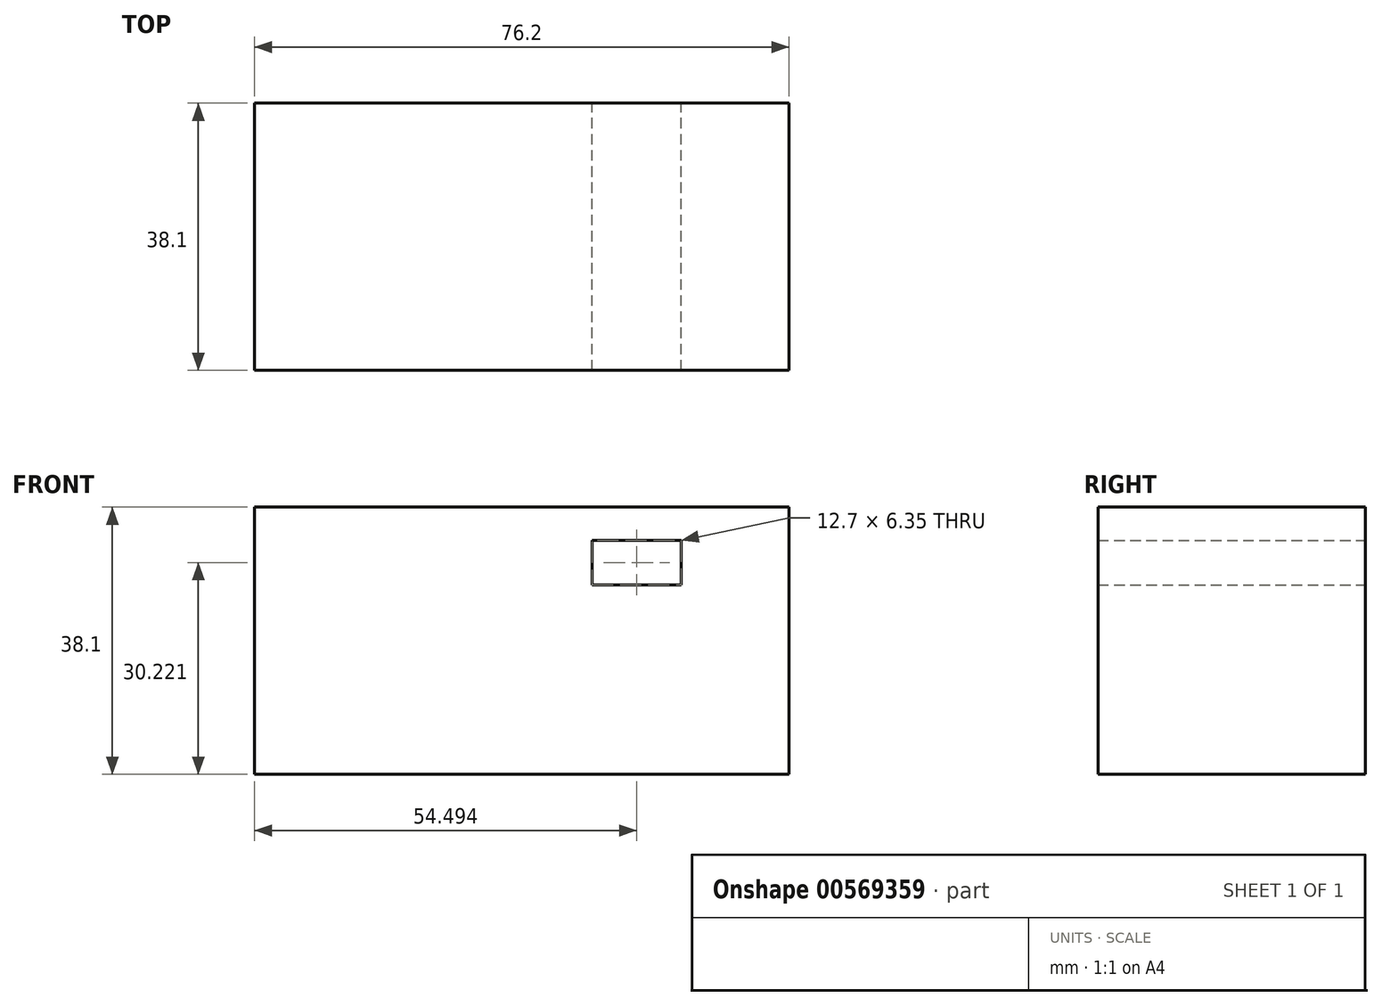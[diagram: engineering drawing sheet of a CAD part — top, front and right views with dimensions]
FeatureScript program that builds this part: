
annotation { "Feature Type Name" : "Feature", "Feature Type Description" : "" }
export const myFeature = defineFeature(function(context is Context, id is Id, definition is map)
    precondition{}
    {
        {
            var Q0;
            Q0=qCreatedBy(makeId("Front.planeOp"),FACE);
            var sketch = newSketch(context, id + "F0", { "sketchPlane" : qUnion([Q0])});
            skLineSegment(sketch, "E0.bottom", {"start": v(38.1, 19.05) * mm, "end": v(-38.1, 19.05) * mm});
            skLineSegment(sketch, "E0.top", {"start": v(38.1, -19.05) * mm, "end": v(-38.1, -19.05) * mm});
            skLineSegment(sketch, "E0.left", {"start": v(38.1, 19.05) * mm, "end": v(38.1, -19.05) * mm});
            skLineSegment(sketch, "E0.right", {"start": v(-38.1, 19.05) * mm, "end": v(-38.1, -19.05) * mm});
            skPoint(sketch, "E0.middle", {"position": v(0, 0) * mm});
            skSolve(sketch);
        }
        {
            var Q0;
            Q0=makeQuery(id+"F0.imprint","IMPRINT",FACE,{"disambiguationData":[TD([[makeQuery(id+"F0.imprint","IMPRINT",EDGE,{"derivedFrom":sQuery(id+"F0.wireOp",EDGE,"E0.bottom")}),1.0]])]});
            var sketch = newSketch(context, id + "F1", { "sketchPlane" : qUnion([Q0])});
            skLineSegment(sketch, "E1.bottom", {"start": v(10.04, 14.35) * mm, "end": v(22.74, 14.35) * mm});
            skLineSegment(sketch, "E1.top", {"start": v(10.04, 8) * mm, "end": v(22.74, 8) * mm});
            skLineSegment(sketch, "E1.left", {"start": v(10.04, 14.35) * mm, "end": v(10.04, 8) * mm});
            skLineSegment(sketch, "E1.right", {"start": v(22.74, 14.35) * mm, "end": v(22.74, 8) * mm});
            skSolve(sketch);
        }
        {
            var Q0;
            Q0=makeQuery(id+"F0.imprint","IMPRINT",FACE,{"disambiguationData":[TD([[makeQuery(id+"F0.imprint","IMPRINT",EDGE,{"derivedFrom":sQuery(id+"F0.wireOp",EDGE,"E0.bottom")}),1.0]])]});
            extrude(context, id + "F2", {"entities" : qUnion([Q0]), "depth" : 38.1 * mm, "offsetDistance" : 25.4 * mm});
        }
        {
            var Q0;
            Q0=makeQuery(id+"F1.imprint","IMPRINT",FACE,{"disambiguationData":[TD([[makeQuery(id+"F1.imprint","IMPRINT",EDGE,{"derivedFrom":sQuery(id+"F1.wireOp",EDGE,"E1.bottom")}),-1.0]])]});
            extrude(context, id + "F3", {"entities" : qUnion([Q0]), "operationType" : NewBodyOperationType.REMOVE, "depth" : 64.52 * mm, "offsetDistance" : 25.4 * mm});
        }
    });
